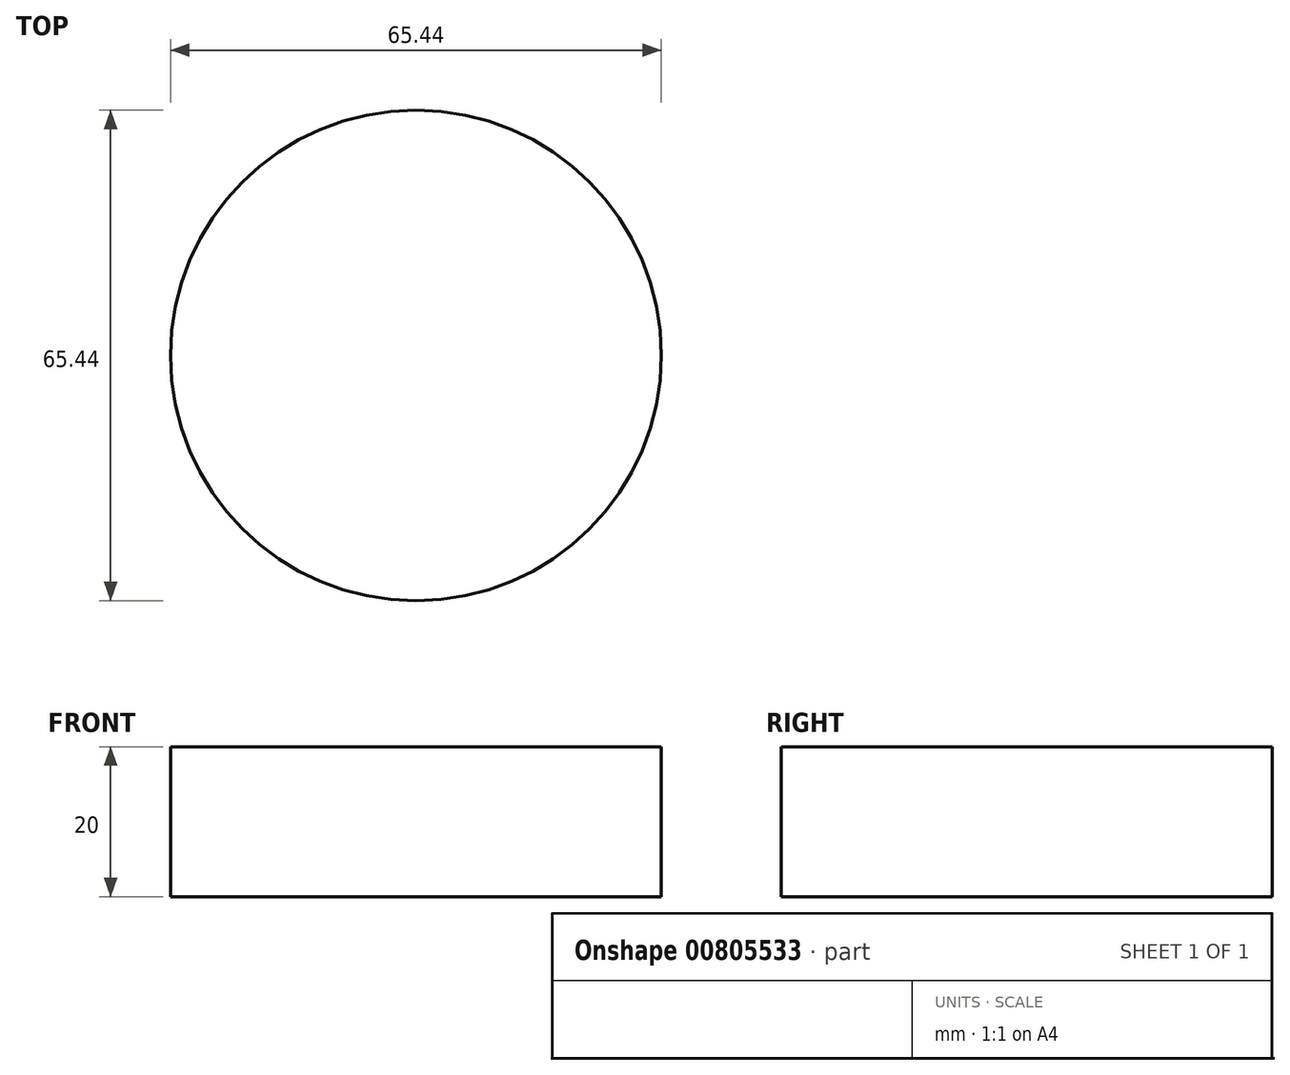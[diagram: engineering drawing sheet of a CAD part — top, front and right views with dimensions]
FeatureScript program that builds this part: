
annotation { "Feature Type Name" : "Feature", "Feature Type Description" : "" }
export const myFeature = defineFeature(function(context is Context, id is Id, definition is map)
    precondition{}
    {
        {
            var Q0;
            Q0=qCreatedBy(makeId("Top.planeOp"),FACE);
            var sketch = newSketch(context, id + "F0", { "sketchPlane" : qUnion([Q0])});
            skCircle(sketch, "E0", {"center": v(0, 0) * mm, "radius": 32.72 * mm});
            skSolve(sketch);
        }
        {
            var Q0;
            Q0 = qSketchRegion(id + "F0", true);
            extrude(context, id + "F1", {"entities" : qUnion([Q0]), "depth" : 20 * mm, "offsetDistance" : 25.4 * mm});
        }
    });
